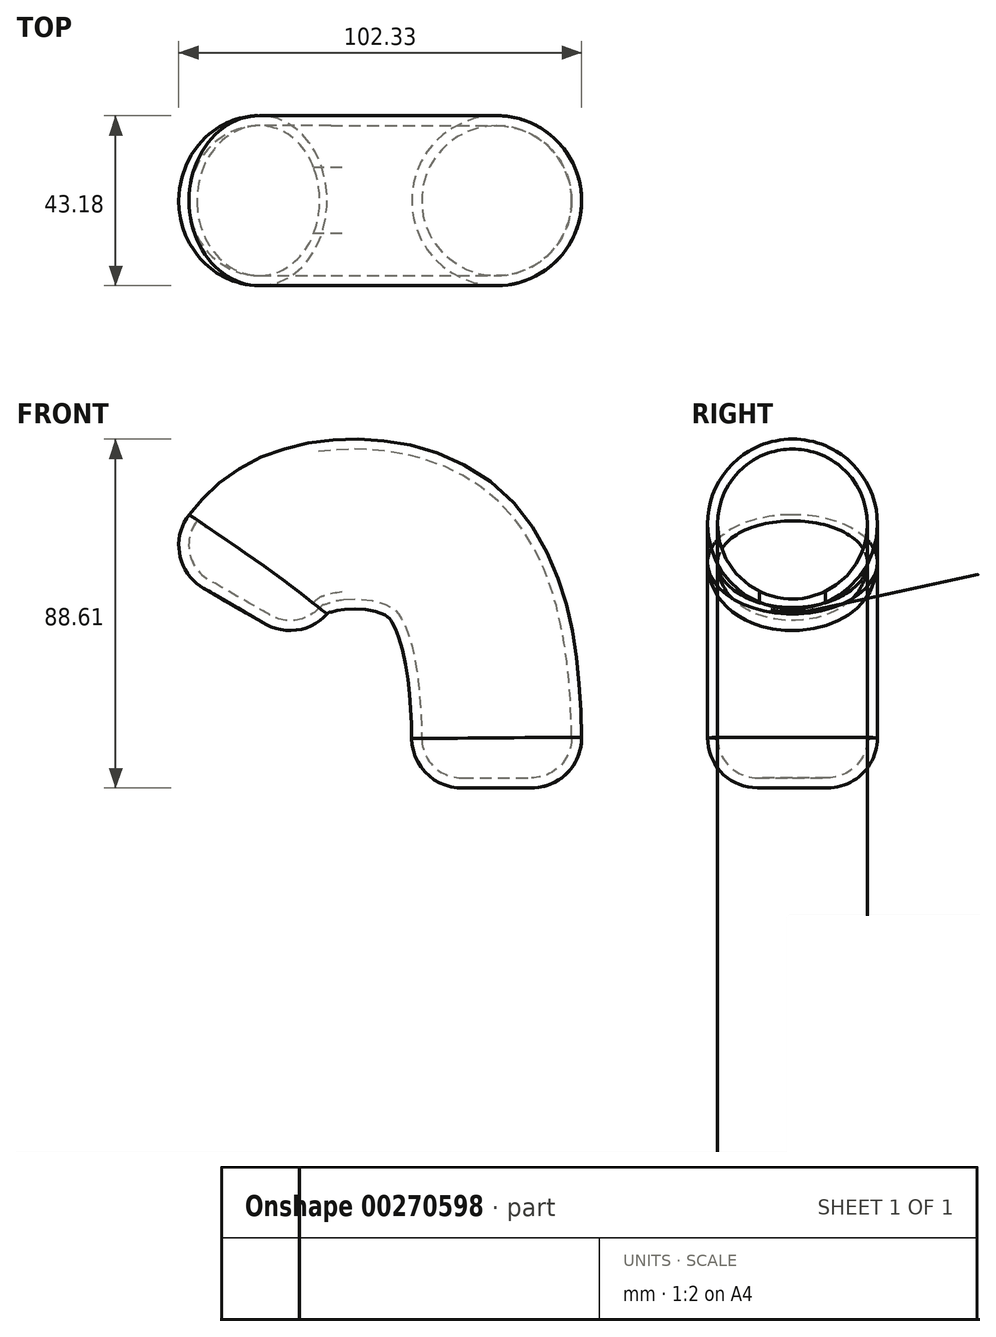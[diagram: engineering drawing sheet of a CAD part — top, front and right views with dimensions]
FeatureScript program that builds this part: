
annotation { "Feature Type Name" : "Feature", "Feature Type Description" : "" }
export const myFeature = defineFeature(function(context is Context, id is Id, definition is map)
    precondition{}
    {
        {
            var Q0;
            Q0=qCreatedBy(makeId("Top.planeOp"),FACE);
            var sketch = newSketch(context, id + "F0", { "sketchPlane" : qUnion([Q0])});
            skCircle(sketch, "E0", {"center": v(0, 0) * mm, "radius": 21.59 * mm});
            skSolve(sketch);
        }
        {
            var Q0;
            Q0=qCreatedBy(makeId("Front.planeOp"),FACE);
            var sketch = newSketch(context, id + "F1", { "sketchPlane" : qUnion([Q0])});
            skFitSpline(sketch, "E1", {"points": [v(0, 0) * mm, v(-13.73, 60) * mm, v(-50.8, 64.35) * mm, v(-67.17, 46.57) * mm], "startDerivative": vector(5.04, 176.59) * mm, "endDerivative": vector(-60.45, -97.87) * mm});
            skSolve(sketch);
        }
        {
            var Q0;
            Q0=makeQuery(id+"F0.imprint","IMPRINT",FACE,{"disambiguationData":[TD([[makeQuery(id+"F0.imprint","IMPRINT",EDGE,{"derivedFrom":sQuery(id+"F0.wireOp",EDGE,"E0")}),1.0]])]});
            var Q1;
            Q1=sQuery(id+"F1.wireOp",EDGE,"E1");
            sweep(context, id + "F2", {"profiles" : qUnion([Q0]), "path" : qUnion([Q1])});
        }
        {
            var Q0;
            Q0=makeQuery(id+"F2.opSweep","SWEPT_FACE",FACE,{"disambiguationData":[OSD([sQuery(id+"F0.wireOp",EDGE,"E0"),sQuery(id+"F1.wireOp",EDGE,"E1")])]});
            var Q1;
            Q1=makeQuery(id+"F2.opSweep","CAP_FACE",FACE,{"disambiguationData":[OSD([sQuery(id+"F0.wireOp",EDGE,"E0"),sQuery(id+"F1.wireOp",VERTEX,"E1.end")])],"isStart":false});
            fillet(context, id + "F3", {"entities" : qUnion([Q0, Q1]), "radius" : 12.7 * mm, "tangentPropagation" : true, "allowEdgeOverflow" : false});
        }
        {
            var Q0;
            Q0=makeQuery(id+"F2.opSweep","SWEPT_FACE",FACE,{"disambiguationData":[OSD([sQuery(id+"F0.wireOp",EDGE,"E0"),sQuery(id+"F1.wireOp",EDGE,"E1")])]});
            var Q1;
            Q1=makeQuery(id+"F3.opFillet","BLEND_FACE",FACE,{"disambiguationData":[OSD([sQuery(id+"F0.wireOp",EDGE,"E0"),sQuery(id+"F1.wireOp",VERTEX,"E1.end")])]});
            var Q2;
            Q2=makeQuery(id+"F3.opFillet","BLEND_FACE",FACE,{"disambiguationData":[OSD([sQuery(id+"F0.wireOp",EDGE,"E0"),sQuery(id+"F1.wireOp",VERTEX,"E1.start")])]});
            var Q3;
            Q3=makeQuery(id+"F2.opSweep","SWEPT_BODY",BODY,{"disambiguationData":[OSD([sQuery(id+"F0.wireOp",EDGE,"E0"),sQuery(id+"F1.wireOp",EDGE,"E1")])]});
            shell(context, id + "F4", {"isHollow" : true, "entities" : qUnion([Q0, Q1, Q2]), "parts" : qUnion([Q3]), "thickness" : 2.54 * mm});
        }
    });
